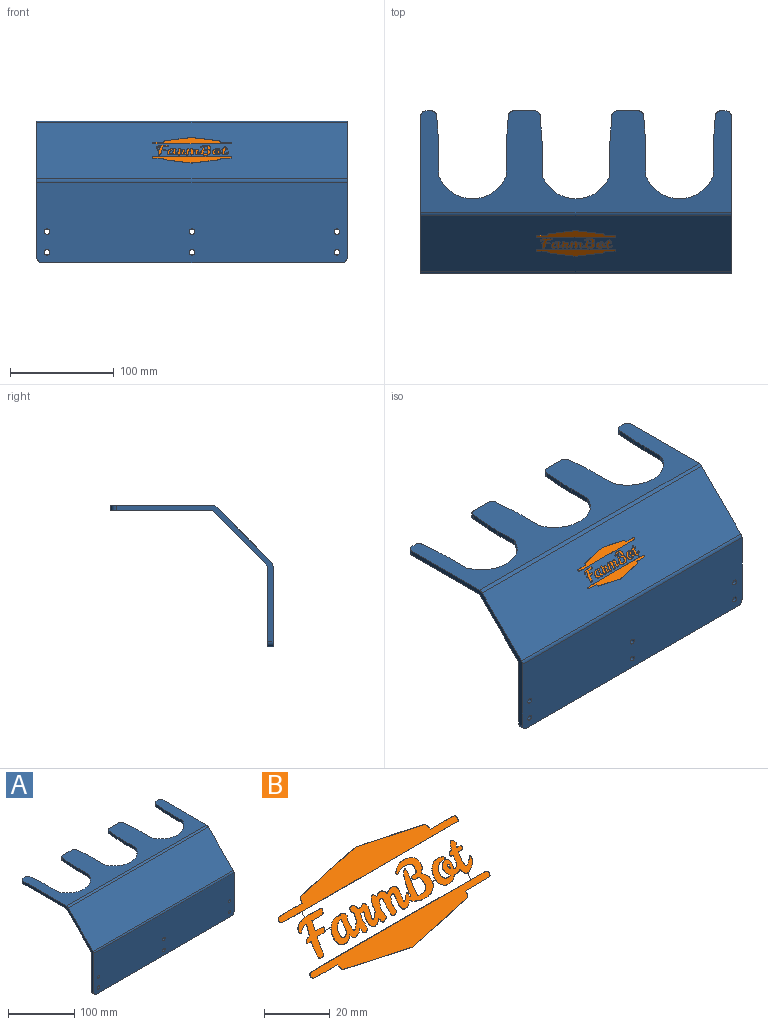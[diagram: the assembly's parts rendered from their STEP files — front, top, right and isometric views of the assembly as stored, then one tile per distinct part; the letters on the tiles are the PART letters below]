
ASSEMBLY  parts=2 mates=1
PART A: 52 faces, bbox 300x156.6x136.6 mm
  f0: plane 300x97.93mm, normal (0,0,-1), area 13697.5mm2, adj f1,f3,f4,f5,f6,f7,f8,f9
  f1: plane 5.36x5mm, normal (0,1,0), area 26.8mm2, adj f0,f2,f33,f44
  f2: plane 300x97.93mm, normal (0,0,1), area 13697.5mm2, adj f1,f3,f4,f5,f6,f7,f8,f9
  f3: plane 20.73x5mm, normal (0,1,0), area 103.6mm2, adj f0,f2,f24,f34
  f4: plane 20.73x5mm, normal (0,1,0), area 103.6mm2, adj f0,f2,f15,f25
  f5: plane 5.36x5mm, normal (0,1,0), area 26.8mm2, adj f0,f2,f16,f43
  f6: plane 151.57x131.57mm, normal (-1,0,0), area 1228.2mm2, adj f0,f2,f35,f36,f37,f38,f40,f41
  f7: plane 151.57x131.57mm, normal (1,0,0), area 1228.2mm2, adj f0,f2,f35,f36,f37,f38,f40,f42
  f8: plane 20.82x5mm, normal (-1,0.08,0), area 104.4mm2, adj f0,f2,f14,f15
  f9: plane 20.82x5mm, normal (1,0.08,0), area 104.4mm2, adj f0,f2,f13,f16
  f10: plane 22.43x5mm, normal (1,0,0), area 112.2mm2, adj f0,f2,f11,f13
  f11: cylinder r=35mm len=65mm, axis (0,0,1), area 416.7mm2, adj f0,f2,f10,f12
  f12: plane 22.43x5mm, normal (-1,0,0), area 112.2mm2, adj f0,f2,f11,f14
  f13: cylinder r=200mm len=15.11mm, axis (0,0,1), area 75.6mm2, adj f0,f2,f9,f10
  f14: cylinder r=200mm len=15.11mm, axis (0,0,1), area 75.6mm2, adj f0,f2,f8,f12
  f15: cylinder r=5mm len=5mm, axis (0,0,1), area 37.4mm2, adj f0,f2,f4,f8
  f16: cylinder r=5mm len=5mm, axis (0,0,-1), area 37.4mm2, adj f0,f2,f5,f9
  f17: plane 20.82x5mm, normal (-1,0.08,0), area 104.4mm2, adj f0,f2,f23,f24
  f18: plane 20.82x5mm, normal (1,0.08,0), area 104.4mm2, adj f0,f2,f22,f25
  f19: plane 22.43x5mm, normal (1,0,0), area 112.2mm2, adj f0,f2,f20,f22
  f20: cylinder r=35mm len=65mm, axis (0,0,1), area 416.7mm2, adj f0,f2,f19,f21
  f21: plane 22.43x5mm, normal (-1,0,0), area 112.2mm2, adj f0,f2,f20,f23
  f22: cylinder r=200mm len=15.11mm, axis (0,0,1), area 75.6mm2, adj f0,f2,f18,f19
  f23: cylinder r=200mm len=15.11mm, axis (0,0,1), area 75.6mm2, adj f0,f2,f17,f21
  f24: cylinder r=5mm len=5mm, axis (0,0,1), area 37.4mm2, adj f0,f2,f3,f17
  f25: cylinder r=5mm len=5mm, axis (0,0,-1), area 37.4mm2, adj f0,f2,f4,f18
  f26: plane 20.82x5mm, normal (-1,0.08,0), area 104.4mm2, adj f0,f2,f32,f33
  f27: plane 20.82x5mm, normal (1,0.08,0), area 104.4mm2, adj f0,f2,f31,f34
  f28: plane 22.43x5mm, normal (1,0,0), area 112.2mm2, adj f0,f2,f29,f31
  f29: cylinder r=35mm len=65mm, axis (0,0,1), area 416.7mm2, adj f0,f2,f28,f30
  f30: plane 22.43x5mm, normal (-1,0,0), area 112.2mm2, adj f0,f2,f29,f32
  f31: cylinder r=200mm len=15.11mm, axis (0,0,1), area 75.6mm2, adj f0,f2,f27,f28
  f32: cylinder r=200mm len=15.11mm, axis (0,0,1), area 75.6mm2, adj f0,f2,f26,f30
  f33: cylinder r=5mm len=5mm, axis (0,0,1), area 37.4mm2, adj f0,f1,f2,f26
  f34: cylinder r=5mm len=5mm, axis (0,0,-1), area 37.4mm2, adj f0,f2,f3,f27
  f35: plane 300x53.64mm, normal (0,0.71,-0.71), area 22757.4mm2, adj f0,f6,f7,f37
  f36: plane 300x53.64mm, normal (0,-0.71,0.71), area 22757.4mm2, adj f6,f7,f40,f45
  f37: plane 300x77.93mm, normal (0,1,0), area 23238.1mm2, adj f6,f7,f35,f39,f41,f42,f46,f47
  f38: plane 300x77.93mm, normal (0,-1,0), area 23238.1mm2, adj f6,f7,f39,f40,f41,f42,f46,f47
  f39: plane 290x5mm, normal (0,0,-1), area 1450mm2, adj f37,f38,f41,f42
  f40: cylinder r=5mm len=300mm, axis (1,0,0), area 1178.1mm2, adj f6,f7,f36,f38
  f41: cylinder r=5mm len=5mm, axis (0,1,0), area 39.3mm2, adj f6,f37,f38,f39
  f42: cylinder r=5mm len=5mm, axis (0,-1,0), area 39.3mm2, adj f7,f37,f38,f39
  f43: cylinder r=5mm len=5mm, axis (0,0,-1), area 39.3mm2, adj f0,f2,f5,f6
  f44: cylinder r=5mm len=5mm, axis (0,0,1), area 39.3mm2, adj f0,f1,f2,f7
  f45: cylinder r=5mm len=300mm, axis (1,0,0), area 1178.1mm2, adj f2,f6,f7,f36
  f46: cylinder r=2.62mm len=5.25mm, axis (0,-1,0), area 82.5mm2, adj f37,f38
  f47: cylinder r=2.62mm len=5.25mm, axis (0,-1,0), area 82.5mm2, adj f37,f38
  f48: cylinder r=2.62mm len=5.25mm, axis (0,-1,0), area 82.5mm2, adj f37,f38
  f49: cylinder r=2.62mm len=5.25mm, axis (0,-1,0), area 82.5mm2, adj f37,f38
  f50: cylinder r=2.62mm len=5.25mm, axis (0,-1,0), area 82.5mm2, adj f37,f38
  f51: cylinder r=2.62mm len=5.25mm, axis (0,-1,0), area 82.5mm2, adj f37,f38
PART B: 232 faces, bbox 77x24.9x24.9 mm
  f0: extruded ~0.63x0.63mm, area 0.1mm2, adj f1,f229,f230,f231
  f1: extruded ~0.72x0.72mm, area 0.1mm2, adj f0,f2,f230,f231
  f2: extruded ~0.56x0.56mm, area 0.1mm2, adj f1,f229,f230,f231
  f3: extruded ~1.22x0.3mm, area 0.1mm2, adj f4,f227,f230,f231
  f4: extruded ~0.97x0.97mm, area 0.1mm2, adj f3,f5,f230,f231
  f5: extruded ~2.07x2.07mm, area 0.3mm2, adj f4,f6,f230,f231
  f6: extruded ~1.87x0.7mm, area 0.2mm2, adj f5,f7,f230,f231
  f7: extruded ~0.65x0.65mm, area 0.1mm2, adj f6,f8,f230,f231
  f8: extruded ~1.21x1.21mm, area 0.2mm2, adj f7,f227,f230,f231
  f9: extruded ~6.37x0.14mm, area 0.6mm2, adj f10,f228,f230,f231
  f10: plane 1.72x1.72mm, normal (1,0,0), area 0.2mm2, adj f9,f11,f230,f231
  f11: extruded ~4.13x2.15mm, area 0.5mm2, adj f10,f12,f230,f231
  f12: extruded ~0.88x0.88mm, area 0.1mm2, adj f11,f13,f230,f231
  f13: extruded ~0.93x0.6mm, area 0.1mm2, adj f12,f14,f230,f231
  f14: extruded ~2.2x1mm, area 0.3mm2, adj f13,f15,f230,f231
  f15: extruded ~2.1x2.1mm, area 0.3mm2, adj f14,f16,f230,f231
  f16: extruded ~1.29x1.29mm, area 0.2mm2, adj f15,f17,f230,f231
  f17: extruded ~1.02x0.2mm, area 0.1mm2, adj f16,f18,f230,f231
  f18: extruded ~1.09x0.36mm, area 0.1mm2, adj f17,f19,f230,f231
  f19: extruded ~0.58x0.58mm, area 0.1mm2, adj f18,f20,f230,f231
  f20: extruded ~0.91x0.29mm, area 0.1mm2, adj f19,f21,f230,f231
  f21: extruded ~0.91x0.14mm, area 0.1mm2, adj f20,f22,f230,f231
  f22: extruded ~0.54x0.54mm, area 0.1mm2, adj f21,f23,f230,f231
  f23: plane 0.47x0.47mm, normal (0.87,-0.35,-0.35), area 0.1mm2, adj f22,f24,f230,f231
  f24: plane 0.48x0.48mm, normal (0.91,0.29,0.29), area 0.1mm2, adj f23,f25,f230,f231
  f25: extruded ~2.37x1.45mm, area 0.4mm2, adj f24,f26,f230,f231
  f26: extruded ~0.75x0.6mm, area 0.1mm2, adj f25,f27,f230,f231
  f27: extruded ~0.87x0.75mm, area 0.1mm2, adj f26,f28,f230,f231
  f28: extruded ~0.41x0.4mm, area 0.1mm2, adj f27,f29,f230,f231
  f29: extruded ~0.51x0.12mm, area 0.1mm2, adj f28,f30,f230,f231
  f30: extruded ~0.74x0.74mm, area 0.1mm2, adj f29,f31,f230,f231
  f31: extruded ~1.02x1.02mm, area 0.1mm2, adj f30,f32,f230,f231
  f32: extruded ~1.01x0.93mm, area 0.2mm2, adj f31,f33,f230,f231
  f33: extruded ~0.78x0.28mm, area 0.1mm2, adj f32,f34,f230,f231
  f34: extruded ~0.97x0.97mm, area 0.1mm2, adj f33,f35,f230,f231
  f35: extruded ~1.06x1.06mm, area 0.1mm2, adj f34,f36,f230,f231
  f36: extruded ~1.45x0.55mm, area 0.2mm2, adj f35,f37,f230,f231
  f37: extruded ~3.02x3.02mm, area 0.6mm2, adj f36,f38,f230,f231
  f38: plane 0.45x0.42mm, normal (-0.74,-0.47,-0.47), area 0.1mm2, adj f37,f39,f230,f231
  f39: plane 0.5x0.17mm, normal (-0.27,0.68,0.68), area 0.1mm2, adj f38,f40,f230,f231
  f40: extruded ~2.56x1.49mm, area 0.4mm2, adj f39,f41,f230,f231
  f41: extruded ~2.21x2.21mm, area 0.4mm2, adj f40,f42,f230,f231
  f42: extruded ~1.46x0.26mm, area 0.1mm2, adj f41,f43,f230,f231
  f43: extruded ~1.25x0.42mm, area 0.2mm2, adj f42,f44,f230,f231
  f44: extruded ~3.53x0.65mm, area 0.4mm2, adj f43,f45,f230,f231
  f45: extruded ~3.22x1.99mm, area 0.4mm2, adj f44,f46,f230,f231
  f46: extruded ~1.84x1.84mm, area 0.3mm2, adj f45,f47,f230,f231
  f47: plane 1.41x0.07mm, normal (0,0.71,0.71), area 0.1mm2, adj f46,f48,f230,f231
  f48: extruded ~1.6x1.6mm, area 0.2mm2, adj f47,f49,f230,f231
  f49: extruded ~1.57x1.22mm, area 0.2mm2, adj f48,f50,f230,f231
  f50: extruded ~0.6x0.55mm, area 0.1mm2, adj f49,f51,f230,f231
  f51: extruded ~2.23x2.23mm, area 0.3mm2, adj f50,f52,f230,f231
  f52: extruded ~2.13x1.57mm, area 0.3mm2, adj f51,f53,f230,f231
  f53: extruded ~4.3x0.34mm, area 0.4mm2, adj f52,f54,f230,f231
  f54: extruded ~3.31x1.78mm, area 0.4mm2, adj f53,f55,f230,f231
  f55: extruded ~1.5x0.37mm, area 0.2mm2, adj f54,f56,f230,f231
  f56: extruded ~3.3x0.58mm, area 0.3mm2, adj f55,f57,f230,f231
  f57: extruded ~2.29x1.48mm, area 0.3mm2, adj f56,f58,f230,f231
  f58: extruded ~0.9x0.9mm, area 0.1mm2, adj f57,f59,f230,f231
  f59: extruded ~1.22x0.4mm, area 0.1mm2, adj f58,f60,f230,f231
  f60: extruded ~1.26x0.32mm, area 0.1mm2, adj f59,f61,f230,f231
  f61: extruded ~0.46x0.46mm, area 0.1mm2, adj f60,f62,f230,f231
  f62: extruded ~1.49x0.53mm, area 0.2mm2, adj f61,f63,f230,f231
  f63: extruded ~1.17x0.41mm, area 0.1mm2, adj f62,f64,f230,f231
  f64: extruded ~2.13x2.13mm, area 0.3mm2, adj f63,f65,f230,f231
  f65: extruded ~2.6x1.08mm, area 0.3mm2, adj f64,f66,f230,f231
  f66: extruded ~1.62x0.27mm, area 0.2mm2, adj f65,f67,f230,f231
  f67: extruded ~3.46x3.46mm, area 0.5mm2, adj f66,f68,f230,f231
  f68: extruded ~2.97x2.97mm, area 0.5mm2, adj f67,f69,f230,f231
  f69: extruded ~4.75x4.75mm, area 0.7mm2, adj f68,f70,f230,f231
  f70: extruded ~0.83x0.83mm, area 0.1mm2, adj f69,f71,f230,f231
  f71: extruded ~0.61x0.61mm, area 0.1mm2, adj f70,f72,f230,f231
  f72: extruded ~0.68x0.68mm, area 0.1mm2, adj f71,f73,f230,f231
  f73: extruded ~1.24x0.75mm, area 0.2mm2, adj f72,f74,f230,f231
  f74: extruded ~1.5x0.81mm, area 0.2mm2, adj f73,f75,f230,f231
  f75: extruded ~1.15x1.15mm, area 0.2mm2, adj f74,f76,f230,f231
  f76: extruded ~2.26x2.26mm, area 0.3mm2, adj f75,f77,f230,f231
  f77: extruded ~0.6x0.51mm, area 0.1mm2, adj f76,f78,f230,f231
  f78: extruded ~3.28x0.68mm, area 0.4mm2, adj f77,f79,f230,f231
  f79: plane 0.34x0.3mm, normal (-0.69,0.51,0.51), area 0mm2, adj f78,f80,f230,f231
  f80: plane 0.32x0.32mm, normal (0.97,0.17,0.17), area 0mm2, adj f79,f81,f230,f231
  f81: extruded ~1.07x0.95mm, area 0.2mm2, adj f80,f82,f230,f231
  f82: extruded ~2.28x0.43mm, area 0.2mm2, adj f81,f83,f230,f231
  f83: extruded ~0.61x0.28mm, area 0.1mm2, adj f82,f84,f230,f231
  f84: extruded ~0.5x0.5mm, area 0.1mm2, adj f83,f85,f230,f231
  f85: extruded ~0.79x0.37mm, area 0.1mm2, adj f84,f86,f230,f231
  f86: extruded ~0.81x0.59mm, area 0.1mm2, adj f85,f87,f230,f231
  f87: extruded ~2.36x2.36mm, area 0.3mm2, adj f86,f88,f230,f231
  f88: plane 0.66x0.66mm, normal (-1,0.07,0.07), area 0.1mm2, adj f87,f89,f230,f231
  f89: plane 0.97x0.71mm, normal (-0.68,0.52,0.52), area 0.1mm2, adj f88,f90,f230,f231
  f90: extruded ~1.73x1.73mm, area 0.4mm2, adj f89,f91,f230,f231
  f91: plane 1.46x1.46mm, normal (0.96,-0.19,-0.19), area 0.2mm2, adj f90,f92,f230,f231
  f92: plane 0.5x0.5mm, normal (0.89,0.32,0.32), area 0.1mm2, adj f91,f93,f230,f231
  f93: extruded ~1.57x0.6mm, area 0.2mm2, adj f92,f94,f230,f231
  f94: extruded ~1.25x0.31mm, area 0.1mm2, adj f93,f95,f230,f231
  f95: extruded ~0.64x0.46mm, area 0.1mm2, adj f94,f96,f230,f231
  f96: extruded ~1.51x0.97mm, area 0.2mm2, adj f95,f97,f230,f231
  f97: extruded ~1.19x0.66mm, area 0.2mm2, adj f96,f98,f230,f231
  f98: extruded ~1x1mm, area 0.1mm2, adj f97,f99,f230,f231
  f99: extruded ~0.88x0.88mm, area 0.1mm2, adj f98,f100,f230,f231
  f100: extruded ~0.9x0.9mm, area 0.1mm2, adj f99,f101,f230,f231
  f101: extruded ~2.35x1.75mm, area 0.3mm2, adj f100,f102,f230,f231
  f102: extruded ~1.36x1.36mm, area 0.2mm2, adj f101,f103,f230,f231
  f103: extruded ~1.75x1.75mm, area 0.2mm2, adj f102,f104,f230,f231
  f104: plane 0.67x0.67mm, normal (0.9,-0.31,-0.31), area 0.1mm2, adj f103,f105,f230,f231
  f105: plane 0.39x0.39mm, normal (0.88,0.34,0.34), area 0.1mm2, adj f104,f106,f230,f231
  f106: extruded ~1.9x0.74mm, area 0.2mm2, adj f105,f107,f230,f231
  f107: extruded ~0.83x0.17mm, area 0.1mm2, adj f106,f108,f230,f231
  f108: extruded ~3.74x0.93mm, area 0.4mm2, adj f107,f109,f230,f231
  f109: extruded ~0.68x0.59mm, area 0.1mm2, adj f108,f110,f230,f231
  f110: plane 2.66x0.07mm, normal (0,0.71,0.71), area 0.3mm2, adj f109,f111,f230,f231
  f111: extruded ~0.91x0.91mm, area 0.1mm2, adj f110,f112,f230,f231
  f112: extruded ~1.71x0.2mm, area 0.2mm2, adj f111,f113,f230,f231
  f113: extruded ~1.58x0.23mm, area 0.2mm2, adj f112,f114,f230,f231
  f114: extruded ~1.2x1.2mm, area 0.2mm2, adj f113,f115,f230,f231
  f115: plane 1.06x1.06mm, normal (0.97,-0.17,-0.17), area 0.1mm2, adj f114,f116,f230,f231
  f116: plane 2.3x0.07mm, normal (0,-0.71,-0.71), area 0.2mm2, adj f115,f117,f230,f231
  f117: extruded ~3.04x0.78mm, area 0.4mm2, adj f116,f118,f230,f231
  f118: extruded ~3.07x0.77mm, area 0.4mm2, adj f117,f119,f230,f231
  f119: extruded ~4.14x0.13mm, area 0.4mm2, adj f118,f120,f230,f231
  f120: plane 1.5x1.5mm, normal (1,0,0), area 0.2mm2, adj f119,f121,f230,f231
  f121: extruded ~29.52x0.08mm, area 3mm2, adj f120,f122,f230,f231
  f122: plane 37.73x0.09mm, normal (0,-0.71,-0.71), area 3.8mm2, adj f121,f123,f230,f231
  f123: plane 0.29x0.29mm, normal (0.78,-0.44,-0.44), area 0mm2, adj f122,f124,f230,f231
  f124: extruded ~1x1mm, area 0.1mm2, adj f123,f125,f230,f231
  f125: extruded ~5.86x0.44mm, area 0.6mm2, adj f124,f126,f230,f231
  f126: plane 4.91x0.07mm, normal (0,0.71,0.71), area 0.5mm2, adj f125,f127,f230,f231
  f127: plane 0.53x0.53mm, normal (0.99,0.09,0.09), area 0.1mm2, adj f126,f128,f230,f231
  f128: extruded ~1.23x1.18mm, area 0.2mm2, adj f127,f129,f230,f231
  f129: extruded ~26.13x3.2mm, area 2.7mm2, adj f128,f130,f230,f231
  f130: extruded ~26.71x3.33mm, area 2.7mm2, adj f129,f131,f230,f231
  f131: extruded ~1.23x1.23mm, area 0.2mm2, adj f130,f132,f230,f231
  f132: plane 0.35x0.35mm, normal (-1,0,0), area 0mm2, adj f131,f133,f230,f231
  f133: plane 4.98x0.07mm, normal (0,0.71,0.71), area 0.5mm2, adj f132,f134,f230,f231
  f134: extruded ~5.43x0.23mm, area 0.5mm2, adj f133,f135,f230,f231
  f135: extruded ~1.36x1.36mm, area 0.2mm2, adj f134,f136,f230,f231
  f136: extruded ~8.52x0.16mm, area 0.9mm2, adj f135,f137,f230,f231
  f137: plane 1.5x1.5mm, normal (-1,0,0), area 0.2mm2, adj f136,f138,f230,f231
  f138: extruded ~1.91x0.32mm, area 0.2mm2, adj f137,f139,f230,f231
  f139: extruded ~2.71x1.78mm, area 0.4mm2, adj f138,f140,f230,f231
  f140: extruded ~1.13x0.65mm, area 0.2mm2, adj f139,f141,f230,f231
  f141: extruded ~2.24x0.85mm, area 0.3mm2, adj f140,f142,f230,f231
  f142: extruded ~0.51x0.21mm, area 0.1mm2, adj f141,f143,f230,f231
  f143: extruded ~1.35x1.35mm, area 0.2mm2, adj f142,f144,f230,f231
  f144: plane 1.17x1.17mm, normal (-0.94,0.24,0.24), area 0.2mm2, adj f143,f145,f230,f231
  f145: plane 0.76x0.28mm, normal (-0.36,0.66,0.66), area 0.1mm2, adj f144,f146,f230,f231
  f146: extruded ~1.49x0.94mm, area 0.2mm2, adj f145,f147,f230,f231
  f147: extruded ~0.92x0.24mm, area 0.1mm2, adj f146,f148,f230,f231
  f148: extruded ~0.86x0.26mm, area 0.1mm2, adj f147,f149,f230,f231
  f149: extruded ~3.92x3.92mm, area 0.6mm2, adj f148,f150,f230,f231
  f150: extruded ~1.96x0.27mm, area 0.2mm2, adj f149,f151,f230,f231
  f151: extruded ~0.85x0.85mm, area 0.1mm2, adj f150,f152,f230,f231
  f152: extruded ~2.71x2.71mm, area 0.4mm2, adj f151,f153,f230,f231
  f153: plane 0.89x0.89mm, normal (0.97,-0.16,-0.16), area 0.1mm2, adj f152,f154,f230,f231
  f154: plane 1.64x0.13mm, normal (-0.05,-0.71,-0.71), area 0.2mm2, adj f153,f155,f230,f231
  f155: extruded ~1.81x0.18mm, area 0.2mm2, adj f154,f156,f230,f231
  f156: extruded ~0.27x0.27mm, area 0mm2, adj f155,f157,f230,f231
  f157: plane 2.66x0.07mm, normal (0,-0.71,-0.71), area 0.3mm2, adj f156,f158,f230,f231
  f158: extruded ~2.39x2.39mm, area 0.4mm2, adj f157,f159,f230,f231
  f159: extruded ~1.69x1.69mm, area 0.2mm2, adj f158,f160,f230,f231
  f160: extruded ~4.82x0.87mm, area 0.5mm2, adj f159,f161,f230,f231
  f161: plane 0.39x0.39mm, normal (0.77,-0.45,-0.45), area 0.1mm2, adj f160,f162,f230,f231
  f162: plane 0.49x0.49mm, normal (-0.93,-0.25,-0.25), area 0.1mm2, adj f161,f163,f230,f231
  f163: extruded ~1.58x0.71mm, area 0.2mm2, adj f162,f164,f230,f231
  f164: extruded ~2.2x0.91mm, area 0.3mm2, adj f163,f165,f230,f231
  f165: plane 0.56x0.43mm, normal (0.68,-0.52,-0.52), area 0.1mm2, adj f164,f166,f230,f231
  f166: plane 0.55x0.55mm, normal (-0.99,-0.09,-0.09), area 0.1mm2, adj f165,f167,f230,f231
  f167: extruded ~0.97x0.97mm, area 0.2mm2, adj f166,f168,f230,f231
  f168: extruded ~1.35x0.52mm, area 0.2mm2, adj f167,f169,f230,f231
  f169: extruded ~1.24x1.24mm, area 0.2mm2, adj f168,f170,f230,f231
  f170: extruded ~1.77x1.77mm, area 0.2mm2, adj f169,f171,f230,f231
  f171: plane 0.76x0.76mm, normal (0.97,-0.17,-0.17), area 0.1mm2, adj f170,f172,f230,f231
  f172: plane 0.75x0.1mm, normal (0.05,-0.71,-0.71), area 0.1mm2, adj f171,f173,f230,f231
  f173: plane 0.75x0.1mm, normal (0.05,-0.71,-0.71), area 0.1mm2, adj f172,f174,f230,f231
  f174: plane 0.35x0.35mm, normal (-0.89,0.32,0.32), area 0mm2, adj f173,f175,f230,f231
  f175: extruded ~2.98x2.98mm, area 0.4mm2, adj f174,f176,f230,f231
  f176: extruded ~1.51x0.79mm, area 0.2mm2, adj f175,f177,f230,f231
  f177: extruded ~2.11x0.76mm, area 0.2mm2, adj f176,f178,f230,f231
  f178: plane 0.54x0.44mm, normal (0.69,-0.51,-0.51), area 0.1mm2, adj f177,f179,f230,f231
  f179: plane 0.52x0.52mm, normal (-0.99,-0.1,-0.1), area 0.1mm2, adj f178,f180,f230,f231
  f180: extruded ~1.78x0.83mm, area 0.3mm2, adj f179,f181,f230,f231
  f181: extruded ~1.22x1.22mm, area 0.2mm2, adj f180,f182,f230,f231
  f182: extruded ~2.13x2.13mm, area 0.3mm2, adj f181,f183,f230,f231
  f183: extruded ~1.53x1.31mm, area 0.2mm2, adj f182,f184,f230,f231
  f184: extruded ~1.54x1.54mm, area 0.2mm2, adj f183,f185,f230,f231
  f185: extruded ~3.02x3.02mm, area 0.4mm2, adj f184,f186,f230,f231
  f186: extruded ~1.82x0.37mm, area 0.2mm2, adj f185,f187,f230,f231
  f187: extruded ~0.71x0.71mm, area 0.1mm2, adj f186,f188,f230,f231
  f188: extruded ~0.92x0.92mm, area 0.1mm2, adj f187,f189,f230,f231
  f189: extruded ~1.87x1.87mm, area 0.3mm2, adj f188,f190,f230,f231
  f190: extruded ~1.33x0.75mm, area 0.2mm2, adj f189,f191,f230,f231
  f191: extruded ~1.63x1.63mm, area 0.2mm2, adj f190,f192,f230,f231
  f192: extruded ~2.62x2.62mm, area 0.5mm2, adj f191,f193,f230,f231
  f193: extruded ~1.85x0.76mm, area 0.2mm2, adj f192,f194,f230,f231
  f194: plane 0.5x0.39mm, normal (0.67,-0.52,-0.52), area 0.1mm2, adj f193,f195,f230,f231
  f195: plane 0.66x0.39mm, normal (-0.56,-0.59,-0.59), area 0.1mm2, adj f194,f196,f230,f231
  f196: extruded ~3.14x0.92mm, area 0.3mm2, adj f195,f197,f230,f231
  f197: extruded ~4.39x0.32mm, area 0.4mm2, adj f196,f198,f230,f231
  f198: extruded ~2.4x1.49mm, area 0.3mm2, adj f197,f199,f230,f231
  f199: extruded ~0.76x0.76mm, area 0.1mm2, adj f198,f200,f230,f231
  f200: plane 1.41x0.07mm, normal (0,-0.71,-0.71), area 0.1mm2, adj f199,f201,f230,f231
  f201: extruded ~0.73x0.73mm, area 0.1mm2, adj f200,f202,f230,f231
  f202: extruded ~2.22x1.53mm, area 0.3mm2, adj f201,f203,f230,f231
  f203: extruded ~1.43x0.13mm, area 0.1mm2, adj f202,f204,f230,f231
  f204: extruded ~2.77x0.81mm, area 0.3mm2, adj f203,f205,f230,f231
  f205: extruded ~1.43x0.37mm, area 0.2mm2, adj f204,f206,f230,f231
  f206: extruded ~1.43x0.27mm, area 0.1mm2, adj f205,f207,f230,f231
  f207: extruded ~0.69x0.43mm, area 0.1mm2, adj f206,f208,f230,f231
  f208: extruded ~1.09x1.03mm, area 0.2mm2, adj f207,f209,f230,f231
  f209: extruded ~0.4x0.11mm, area 0mm2, adj f208,f210,f230,f231
  f210: plane 1.72x1.72mm, normal (-1,0,0), area 0.2mm2, adj f209,f211,f230,f231
  f211: extruded ~31.4x0.1mm, area 3.1mm2, adj f210,f212,f230,f231
  f212: extruded ~37.82x0.23mm, area 3.8mm2, adj f211,f213,f230,f231
  f213: extruded ~0.99x0.99mm, area 0.2mm2, adj f212,f214,f230,f231
  f214: extruded ~5.85x0.56mm, area 0.6mm2, adj f213,f215,f230,f231
  f215: plane 5.03x0.07mm, normal (0,-0.71,-0.71), area 0.5mm2, adj f214,f216,f230,f231
  f216: plane 0.53x0.53mm, normal (-0.99,-0.08,-0.08), area 0.1mm2, adj f215,f217,f230,f231
  f217: extruded ~1.05x1.05mm, area 0.2mm2, adj f216,f218,f230,f231
  f218: extruded ~12.8x1.72mm, area 1.3mm2, adj f217,f219,f230,f231
  f219: extruded ~13.12x1.67mm, area 1.3mm2, adj f218,f220,f230,f231
  f220: extruded ~0.65x0.17mm, area 0.1mm2, adj f219,f221,f230,f231
  f221: extruded ~26.53x3.34mm, area 2.7mm2, adj f220,f222,f230,f231
  f222: extruded ~1.15x1.15mm, area 0.2mm2, adj f221,f223,f230,f231
  f223: plane 0.45x0.45mm, normal (1,-0.03,-0.03), area 0.1mm2, adj f222,f224,f230,f231
  f224: plane 10.5x0.16mm, normal (0.01,-0.71,-0.71), area 1.1mm2, adj f223,f225,f230,f231
  f225: plane 0.29x0.29mm, normal (0.78,-0.44,-0.44), area 0mm2, adj f224,f226,f230,f231
  f226: extruded ~1x1mm, area 0.1mm2, adj f225,f228,f230,f231
  f227: extruded ~2x2mm, area 0.3mm2, adj f3,f8,f230,f231
  f228: extruded ~0.54x0.34mm, area 0.1mm2, adj f9,f226,f230,f231
  f229: extruded ~0.61x0.61mm, area 0.1mm2, adj f0,f2,f230,f231
  f230: plane 77.01x24.78mm, normal (0,-0.71,0.71), area 1191.9mm2, adj f0,f1,f2,f3,f4,f5,f6,f7
  f231: plane 77.01x24.78mm, normal (0,0.71,-0.71), area 1191.9mm2, adj f0,f1,f2,f3,f4,f5,f6,f7
PLACE A t=(0.08,-0.32,-0.32)mm
PLACE B at identity
MATE fastened A.f36 <-> B.f231  axis (0,-0.71,0.71) through (0.08,-78.6,-23.6)mm
